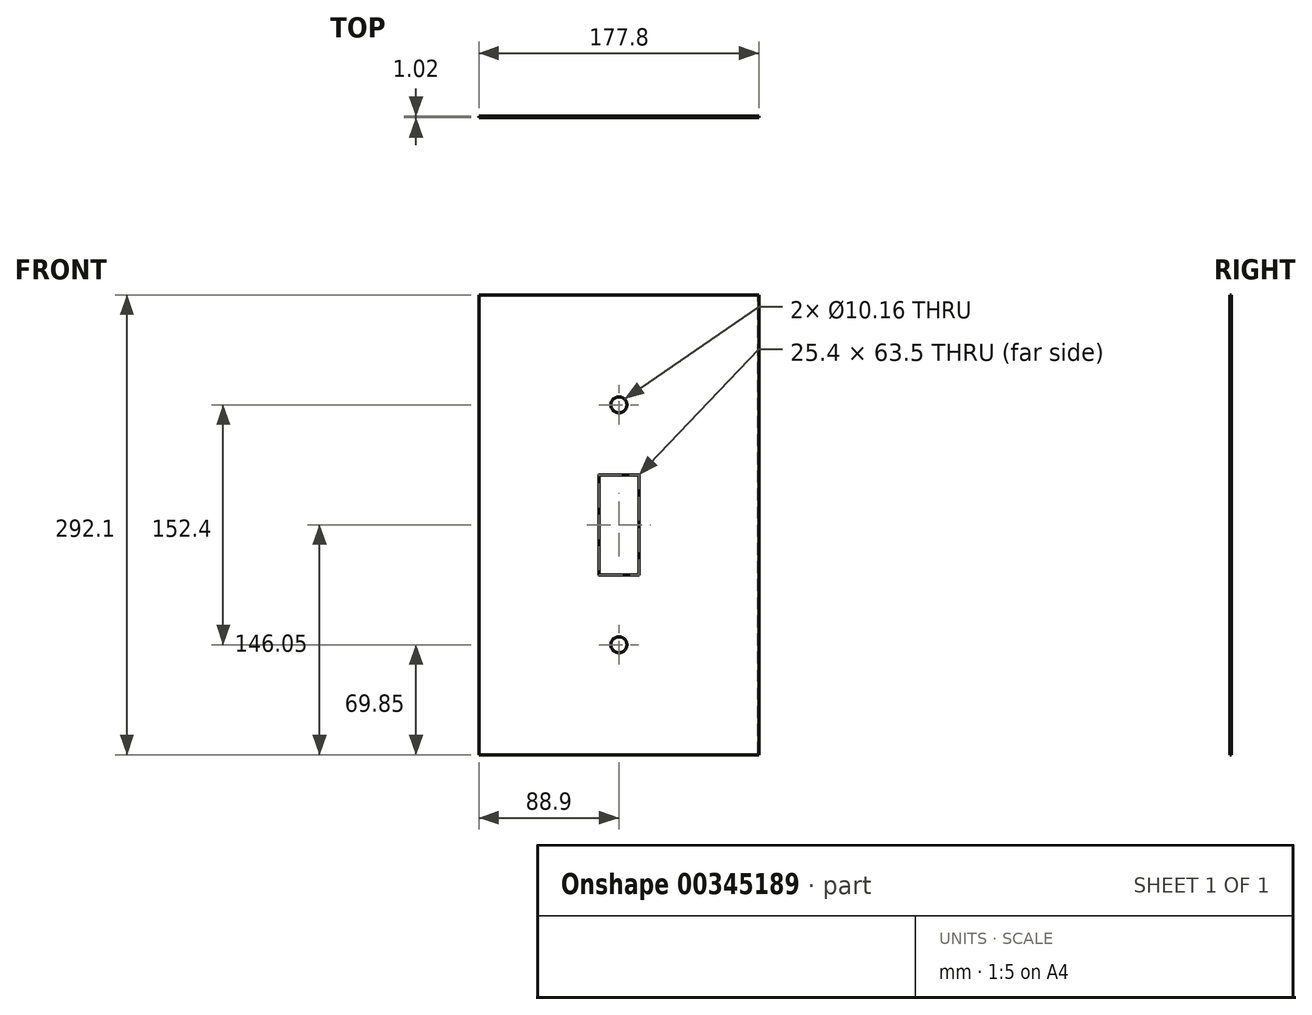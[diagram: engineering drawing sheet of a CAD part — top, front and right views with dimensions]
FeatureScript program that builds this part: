
annotation { "Feature Type Name" : "Feature", "Feature Type Description" : "" }
export const myFeature = defineFeature(function(context is Context, id is Id, definition is map)
    precondition{}
    {
        {
            var Q0;
            Q0=qCreatedBy(makeId("Front.planeOp"),FACE);
            var sketch = newSketch(context, id + "F0", { "sketchPlane" : qUnion([Q0])});
            skLineSegment(sketch, "E0.bottom", {"start": v(0, 0) * mm, "end": v(177.8, 0) * mm});
            skLineSegment(sketch, "E0.top", {"start": v(0, 292.1) * mm, "end": v(177.8, 292.1) * mm});
            skLineSegment(sketch, "E0.left", {"start": v(0, 0) * mm, "end": v(0, 292.1) * mm});
            skLineSegment(sketch, "E0.right", {"start": v(177.8, 0) * mm, "end": v(177.8, 292.1) * mm});
            skSolve(sketch);
        }
        {
            var Q0;
            Q0=makeQuery(id+"F0.imprint","IMPRINT",FACE,{"disambiguationData":[TD([[makeQuery(id+"F0.imprint","IMPRINT",EDGE,{"derivedFrom":sQuery(id+"F0.wireOp",EDGE,"E0.bottom")}),1.0]])]});
            extrude(context, id + "F1", {"entities" : qUnion([Q0]), "depth" : 1.02 * mm});
        }
        {
            var Q0;
            Q0=makeQuery(id+"F1.opExtrude","CAP_FACE",FACE,{"disambiguationData":[OSD([sQuery(id+"F0.wireOp",EDGE,"E0.bottom"),sQuery(id+"F0.wireOp",EDGE,"E0.top"),sQuery(id+"F0.wireOp",EDGE,"E0.left"),sQuery(id+"F0.wireOp",EDGE,"E0.right")])],"isStart":false});
            var sketch = newSketch(context, id + "F2", { "sketchPlane" : qUnion([Q0])});
            skSolve(sketch);
        }
        {
            var Q0;
            Q0=makeQuery(id+"F2.imprint","IMPRINT",FACE,{"disambiguationData":[TD([[makeQuery(id+"F2.imprint","IMPRINT",EDGE,{"derivedFrom":makeQuery(id+"F1.opExtrude","CAP_EDGE",EDGE,{"disambiguationData":[OSD([sQuery(id+"F0.wireOp",EDGE,"E0.bottom")])],"isStart":false})}),1.0]])]});
            var sketch = newSketch(context, id + "F3", { "sketchPlane" : qUnion([Q0])});
            skLineSegment(sketch, "E1.bottom", {"start": v(76.2, 177.8) * mm, "end": v(101.6, 177.8) * mm});
            skLineSegment(sketch, "E1.top", {"start": v(76.2, 114.3) * mm, "end": v(101.6, 114.3) * mm});
            skLineSegment(sketch, "E1.left", {"start": v(76.2, 177.8) * mm, "end": v(76.2, 114.3) * mm});
            skLineSegment(sketch, "E1.right", {"start": v(101.6, 177.8) * mm, "end": v(101.6, 114.3) * mm});
            skSolve(sketch);
        }
        {
            var Q0;
            Q0=makeQuery(id+"F3.imprint","IMPRINT",FACE,{"disambiguationData":[TD([[makeQuery(id+"F3.imprint","IMPRINT",EDGE,{"derivedFrom":sQuery(id+"F3.wireOp",EDGE,"E1.bottom")}),-1.0]])]});
            extrude(context, id + "F4", {"entities" : qUnion([Q0]), "operationType" : NewBodyOperationType.REMOVE, "oppositeDirection" : true, "depth" : 25.4 * mm});
        }
        {
            var Q0;
            Q0=makeQuery(id+"F1.opExtrude","CAP_FACE",FACE,{"disambiguationData":[OSD([sQuery(id+"F0.wireOp",EDGE,"E0.bottom"),sQuery(id+"F0.wireOp",EDGE,"E0.top"),sQuery(id+"F0.wireOp",EDGE,"E0.left"),sQuery(id+"F0.wireOp",EDGE,"E0.right")])],"isStart":true});
            shell(context, id + "F5", {"entities" : qUnion([Q0]), "thickness" : 0.5 * mm});
        }
        {
            var Q0;
            Q0=makeQuery(id+"F2.imprint","IMPRINT",FACE,{"disambiguationData":[TD([[makeQuery(id+"F2.imprint","IMPRINT",EDGE,{"derivedFrom":makeQuery(id+"F1.opExtrude","CAP_EDGE",EDGE,{"disambiguationData":[OSD([sQuery(id+"F0.wireOp",EDGE,"E0.bottom")])],"isStart":false})}),1.0]])]});
            var sketch = newSketch(context, id + "F6", { "sketchPlane" : qUnion([Q0])});
            skCircle(sketch, "E2", {"center": v(88.9, 69.85) * mm, "radius": 5.08 * mm});
            skSolve(sketch);
        }
        {
            var Q0;
            Q0=makeQuery(id+"F6.imprint","IMPRINT",FACE,{"disambiguationData":[TD([[makeQuery(id+"F6.imprint","IMPRINT",EDGE,{"derivedFrom":sQuery(id+"F6.wireOp",EDGE,"E2")}),1.0]])]});
            extrude(context, id + "F7", {"entities" : qUnion([Q0]), "operationType" : NewBodyOperationType.REMOVE, "oppositeDirection" : true, "depth" : 25.4 * mm});
        }
        {
            var Q0;
            Q0=makeQuery(id+"F2.imprint","IMPRINT",FACE,{"disambiguationData":[TD([[makeQuery(id+"F2.imprint","IMPRINT",EDGE,{"derivedFrom":makeQuery(id+"F1.opExtrude","CAP_EDGE",EDGE,{"disambiguationData":[OSD([sQuery(id+"F0.wireOp",EDGE,"E0.bottom")])],"isStart":false})}),1.0]])]});
            var sketch = newSketch(context, id + "F8", { "sketchPlane" : qUnion([Q0])});
            skCircle(sketch, "E3", {"center": v(88.9, 222.25) * mm, "radius": 5.08 * mm});
            skSolve(sketch);
        }
        {
            var Q0;
            Q0=makeQuery(id+"F8.imprint","IMPRINT",FACE,{"disambiguationData":[TD([[makeQuery(id+"F8.imprint","IMPRINT",EDGE,{"derivedFrom":sQuery(id+"F8.wireOp",EDGE,"E3")}),1.0]])]});
            extrude(context, id + "F9", {"entities" : qUnion([Q0]), "operationType" : NewBodyOperationType.REMOVE, "oppositeDirection" : true, "depth" : 25.4 * mm});
        }
    });
